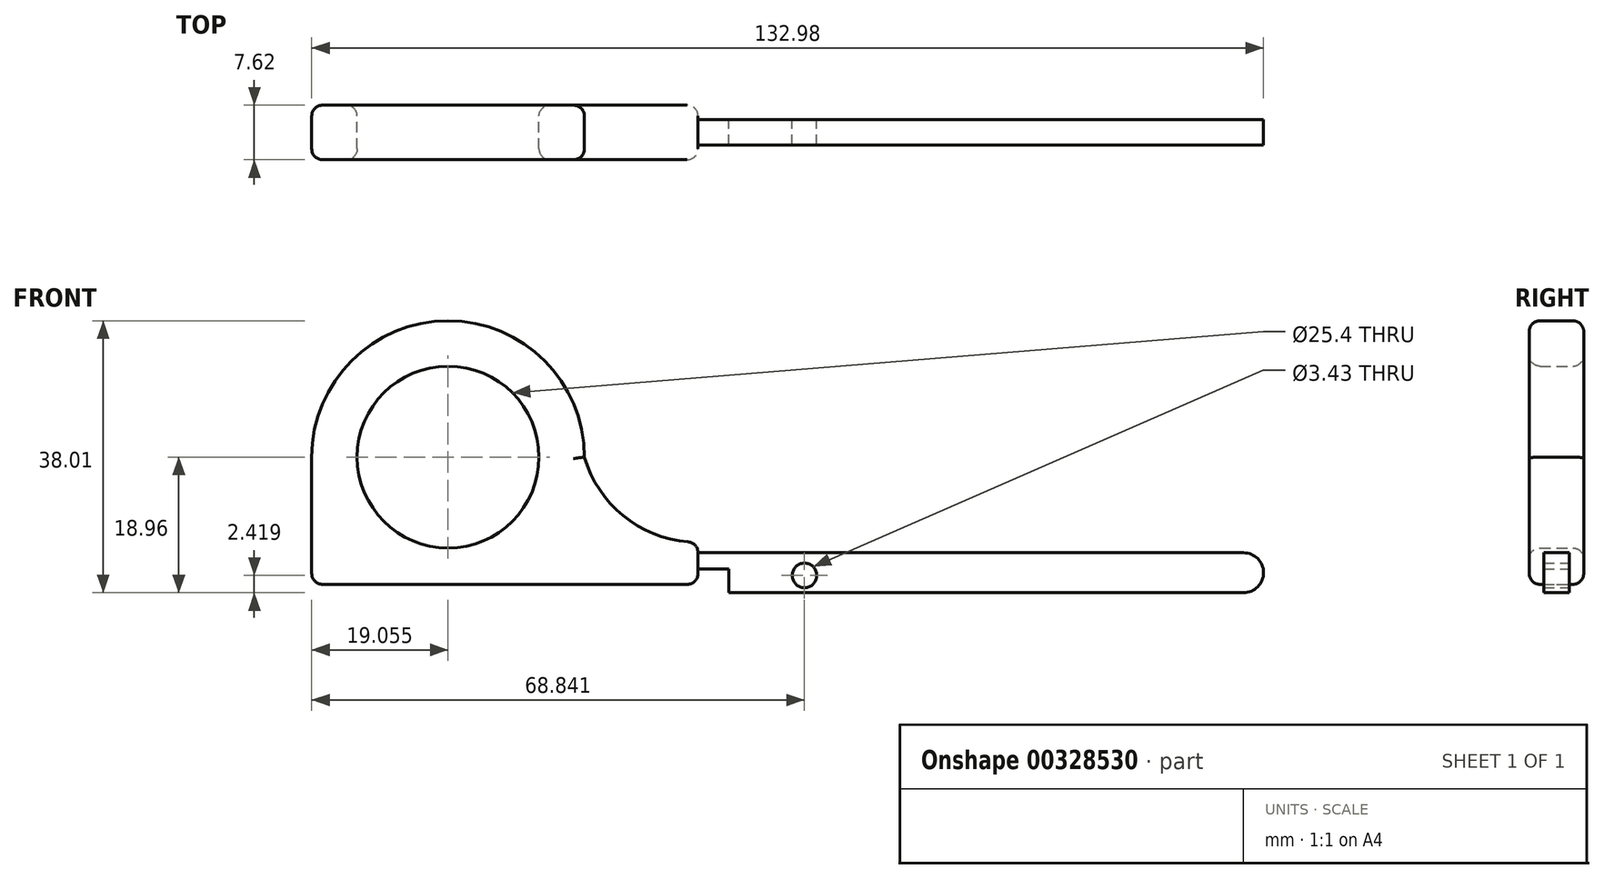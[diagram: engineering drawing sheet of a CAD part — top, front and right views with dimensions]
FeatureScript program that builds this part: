
annotation { "Feature Type Name" : "Feature", "Feature Type Description" : "" }
export const myFeature = defineFeature(function(context is Context, id is Id, definition is map)
    precondition{}
    {
        {
            var Q0;
            Q0=qCreatedBy(makeId("Front.planeOp"),FACE);
            var sketch = newSketch(context, id + "F0", { "sketchPlane" : qUnion([Q0])});
            skCircle(sketch, "E0", {"center": v(-34.92, 8.89) * mm, "radius": 12.7 * mm});
            skArc(sketch, "E1", {"start": v(-53.97, 8.89) * mm, "mid": v(-34.92, 27.94) * mm, "end": v(-15.87, 8.89) * mm});
            skLineSegment(sketch, "E2", {"start": v(-53.98, 8.89) * mm, "end": v(-53.98, -7.37) * mm});
            skLineSegment(sketch, "E3", {"start": v(-52.45, -8.9) * mm, "end": v(-1.52, -8.9) * mm});
            skArc(sketch, "E4", {"start": v(-15.87, 8.89) * mm, "mid": v(-10.48, 0.71) * mm, "end": v(-1.4, -2.97) * mm});
            skLineSegment(sketch, "E5", {"start": v(0, -6.77) * mm, "end": v(4.32, -6.77) * mm});
            skLineSegment(sketch, "E6", {"start": v(76.2, -10.07) * mm, "end": v(4.32, -10.07) * mm});
            skLineSegment(sketch, "E7", {"start": v(4.32, -10.07) * mm, "end": v(4.32, -6.77) * mm});
            skArc(sketch, "E8", {"start": v(76.2, -10.07) * mm, "mid": v(79, -7.28) * mm, "end": v(76.2, -4.48) * mm});
            skCircle(sketch, "E9", {"center": v(14.86, -7.65) * mm, "radius": 1.71 * mm});
            skPoint(sketch, "E10.visualSharp", {"position": v(-53.98, -8.9) * mm});
            skArc(sketch, "E10.filletArc", {"start": v(-53.98, -7.37) * mm, "mid": v(-53.53, -8.44) * mm, "end": v(-52.45, -8.9) * mm});
            skPoint(sketch, "E11.visualSharp", {"position": v(0, -8.9) * mm});
            skArc(sketch, "E11.filletArc", {"start": v(-1.52, -8.9) * mm, "mid": v(-0.44, -8.44) * mm, "end": v(0, -7.37) * mm});
            skPoint(sketch, "E12.visualSharp", {"position": v(0, -3.02) * mm});
            skArc(sketch, "E12.filletArc", {"start": v(0, -4.48) * mm, "mid": v(-0.4, -3.45) * mm, "end": v(-1.4, -2.97) * mm});
            skLineSegment(sketch, "E13", {"start": v(76.2, -4.48) * mm, "end": v(0, -4.48) * mm});
            skLineSegment(sketch, "E14", {"start": v(0, -4.48) * mm, "end": v(0, -7.37) * mm});
            skSolve(sketch);
        }
        {
            var Q0;
            {var subQ0=sQuery(id+"F0.wireOp",EDGE,"E5");Q0=makeQuery(id+"F0.imprint","IMPRINT",FACE,{"disambiguationData":[TD([[makeQuery(id+"F0.imprint","IMPRINT",EDGE,{"derivedFrom":subQ0}),1.0]])]});}
            extrude(context, id + "F1", {"entities" : qUnion([Q0]), "endBound" : BoundingType.SYMMETRIC, "depth" : 3.56 * mm});
        }
        {
            var Q0;
            Q0=makeQuery(id+"F0.imprint","IMPRINT",FACE,{"disambiguationData":[TD([[makeQuery(id+"F0.imprint","IMPRINT",EDGE,{"derivedFrom":sQuery(id+"F0.wireOp",EDGE,"E0")}),-1.0]])]});
            extrude(context, id + "F2", {"entities" : qUnion([Q0]), "endBound" : BoundingType.SYMMETRIC, "depth" : 7.62 * mm});
        }
        {
            var Q0;
            Q0=makeQuery(id+"F2.opExtrude","CAP_EDGE",EDGE,{"disambiguationData":[OSD([sQuery(id+"F0.wireOp",EDGE,"E1")])],"isStart":false});
            var Q1;
            Q1=makeQuery(id+"F2.opExtrude","CAP_EDGE",EDGE,{"disambiguationData":[OSD([sQuery(id+"F0.wireOp",EDGE,"E0")])],"isStart":false});
            var Q2;
            Q2=makeQuery(id+"F2.opExtrude","CAP_EDGE",EDGE,{"disambiguationData":[OSD([sQuery(id+"F0.wireOp",EDGE,"E0")])],"isStart":true});
            var Q3;
            Q3=makeQuery(id+"F2.opExtrude","CAP_EDGE",EDGE,{"disambiguationData":[OSD([sQuery(id+"F0.wireOp",EDGE,"E1")])],"isStart":true});
            fillet(context, id + "F3", {"entities" : qUnion([Q0, Q1, Q2, Q3]), "radius" : 1.52 * mm, "tangentPropagation" : true, "allowEdgeOverflow" : false});
        }
    });
